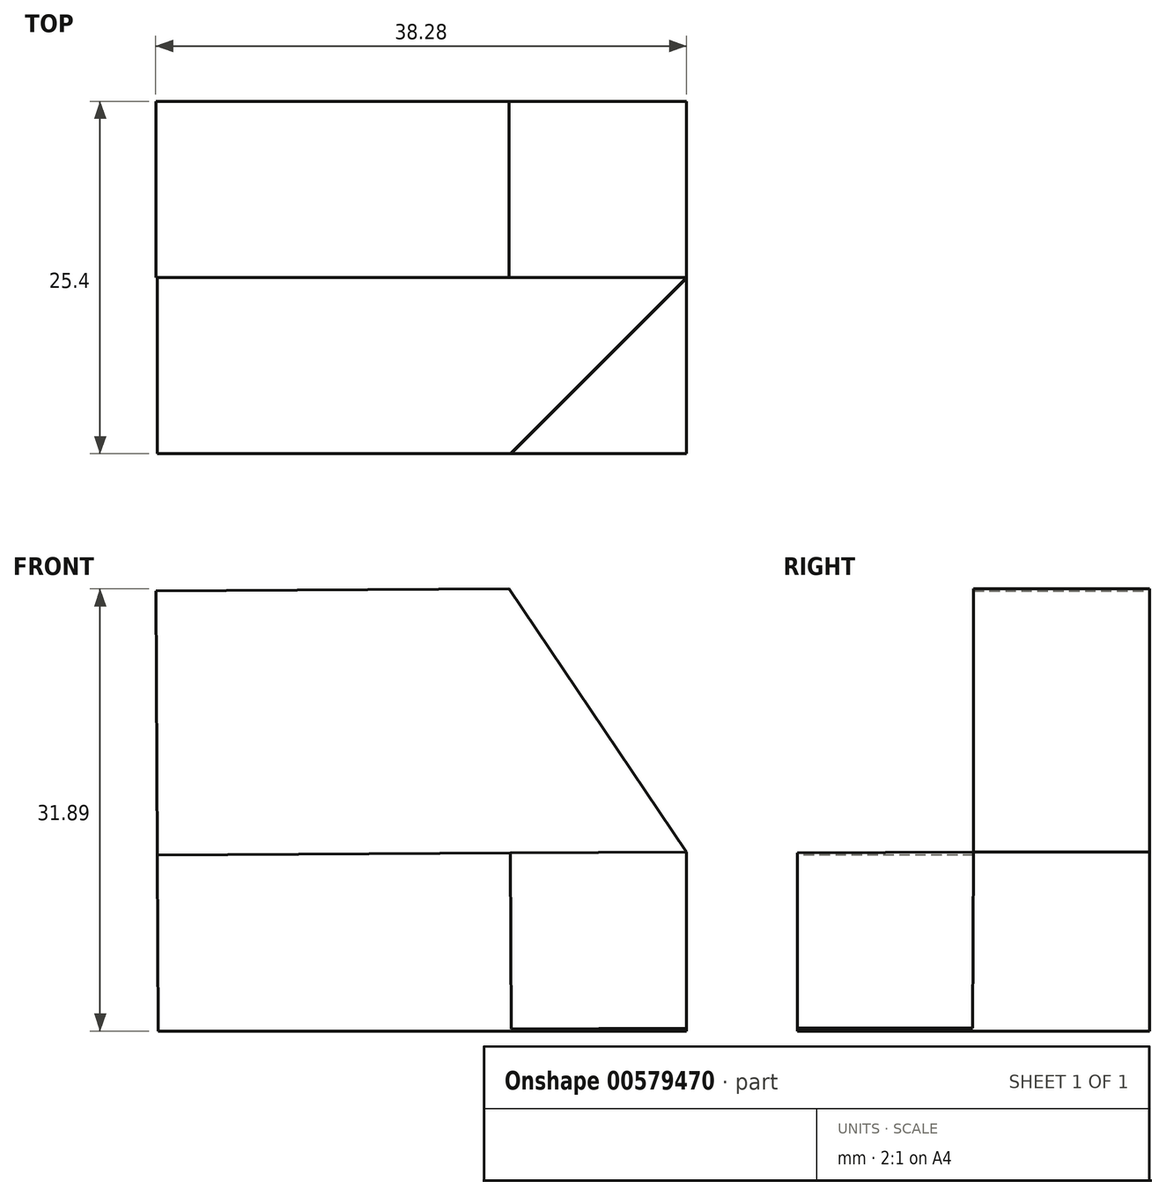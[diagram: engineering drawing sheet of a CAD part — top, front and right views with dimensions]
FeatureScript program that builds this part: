
annotation { "Feature Type Name" : "Feature", "Feature Type Description" : "" }
export const myFeature = defineFeature(function(context is Context, id is Id, definition is map)
    precondition{}
    {
        {
            var Q0;
            Q0=qCreatedBy(makeId("Front.planeOp"),FACE);
            var sketch = newSketch(context, id + "F0", { "sketchPlane" : qUnion([Q0])});
            skLineSegment(sketch, "E0", {"start": v(-42.02, 0) * mm, "end": v(-3.92, 0) * mm});
            skLineSegment(sketch, "E1", {"start": v(-3.92, 0) * mm, "end": v(-3.92, 31.75) * mm});
            skLineSegment(sketch, "E2", {"start": v(-3.92, 31.75) * mm, "end": v(-42.2, 31.75) * mm});
            skLineSegment(sketch, "E3", {"start": v(-42.2, 31.75) * mm, "end": v(-42.02, 0) * mm});
            skLineSegment(sketch, "E4", {"start": v(-42.1, 12.7) * mm, "end": v(-3.92, 12.91) * mm});
            skSolve(sketch);
        }
        {
            var Q0;
            {var subQ0=sQuery(id+"F0.wireOp",EDGE,"E0");Q0=makeQuery(id+"F0.imprint","IMPRINT",FACE,{"disambiguationData":[TD([[makeQuery(id+"F0.imprint","IMPRINT",EDGE,{"derivedFrom":subQ0}),1.0]])]});}
            extrude(context, id + "F1", {"entities" : qUnion([Q0]), "depth" : 25.4 * mm, "offsetDistance" : 25.4 * mm});
        }
        {
            var Q0;
            Q0=makeQuery(id+"F1.opExtrude","SWEPT_FACE",FACE,{"disambiguationData":[OSD([sQuery(id+"F0.wireOp",EDGE,"E4")])]});
            extrude(context, id + "F2", {"entities" : qUnion([Q0]), "operationType" : NewBodyOperationType.ADD, "depth" : 19.05 * mm, "offsetDistance" : 25.4 * mm});
        }
        {
            var Q0;
            {var subQ0=sQuery(id+"F0.wireOp",EDGE,"E4");Q0=makeQuery(id+"F2.boolean.opBoolean","MERGE",FACE,{"derivedFrom":[makeQuery(id+"F1.opExtrude","CAP_FACE",FACE,{"disambiguationData":[OSD([sQuery(id+"F0.wireOp",EDGE,"E0"),sQuery(id+"F0.wireOp",EDGE,"E1"),sQuery(id+"F0.wireOp",EDGE,"E3"),subQ0])],"isStart":false}),makeQuery(id+"F2.opExtrude","SWEPT_FACE",FACE,{"disambiguationData":[OSD([subQ0]),TDD([makeQuery(id+"F1.opExtrude","CAP_EDGE",EDGE,{"disambiguationData":[OSD([subQ0])],"isStart":false})])]})]});}
            var sketch = newSketch(context, id + "F3", { "sketchPlane" : qUnion([Q0])});
            skLineSegment(sketch, "E5", {"start": v(-3.92, 12.91) * mm, "end": v(-42.1, 12.7) * mm});
            skSolve(sketch);
        }
        {
            var Q0;
            Q0 = qSketchRegion(id + "F3", true);
            var Q1;
            {var subQ0=sQuery(id+"F3.wireOp",EDGE,"E5");Q1=makeQuery(id+"F3.imprint","IMPRINT",FACE,{"disambiguationData":[TD([[makeQuery(id+"F3.imprint","IMPRINT",EDGE,{"derivedFrom":subQ0}),-1.0]])]});}
            extrude(context, id + "F4", {"entities" : qUnion([Q0, Q1]), "operationType" : NewBodyOperationType.REMOVE, "oppositeDirection" : true, "depth" : 12.7 * mm, "offsetDistance" : 25.4 * mm});
        }
        {
            var Q0;
            Q0=makeQuery(id+"F4.boolean.opBoolean","COPY",FACE,{"derivedFrom":makeQuery(id+"F4.opExtrude","CAP_FACE",FACE,{"disambiguationData":[OSD([sQuery(id+"F0.wireOp",EDGE,"E1"),sQuery(id+"F0.wireOp",EDGE,"E3"),sQuery(id+"F0.wireOp",EDGE,"E4"),sQuery(id+"F3.wireOp",EDGE,"E5")])],"isStart":false})});
            var sketch = newSketch(context, id + "F5", { "sketchPlane" : qUnion([Q0])});
            skLineSegment(sketch, "E6", {"start": v(-16.73, 31.9) * mm, "end": v(-3.92, 12.91) * mm});
            skSolve(sketch);
        }
        {
            var Q0;
            Q0 = qSketchRegion(id + "F5", true);
            var Q1;
            {var subQ0=sQuery(id+"F5.wireOp",EDGE,"E6");Q1=makeQuery(id+"F5.imprint","IMPRINT",FACE,{"disambiguationData":[TD([[makeQuery(id+"F5.imprint","IMPRINT",EDGE,{"derivedFrom":subQ0}),1.0]])]});}
            extrude(context, id + "F6", {"entities" : qUnion([Q0, Q1]), "operationType" : NewBodyOperationType.REMOVE, "endBound" : BoundingType.THROUGH_ALL, "oppositeDirection" : true, "depth" : 25.4 * mm, "offsetDistance" : 25.4 * mm});
        }
        {
            var Q0;
            Q0=makeQuery(id+"F4.boolean.opBoolean","COPY",FACE,{"derivedFrom":makeQuery(id+"F4.opExtrude","SWEPT_FACE",FACE,{"disambiguationData":[OSD([sQuery(id+"F3.wireOp",EDGE,"E5")])]})});
            var sketch = newSketch(context, id + "F7", { "sketchPlane" : qUnion([Q0])});
            skLineSegment(sketch, "E7", {"start": v(-16.55, -25.4) * mm, "end": v(-3.85, -12.7) * mm});
            skSolve(sketch);
        }
        {
            var Q0;
            Q0 = qSketchRegion(id + "F7", true);
            var Q1;
            {var subQ0=sQuery(id+"F7.wireOp",EDGE,"E7");Q1=makeQuery(id+"F7.imprint","IMPRINT",FACE,{"disambiguationData":[TD([[makeQuery(id+"F7.imprint","IMPRINT",EDGE,{"derivedFrom":subQ0}),-1.0]])]});}
            extrude(context, id + "F8", {"entities" : qUnion([Q0, Q1]), "operationType" : NewBodyOperationType.REMOVE, "oppositeDirection" : true, "depth" : 12.7 * mm, "offsetDistance" : 25.4 * mm});
        }
    });
